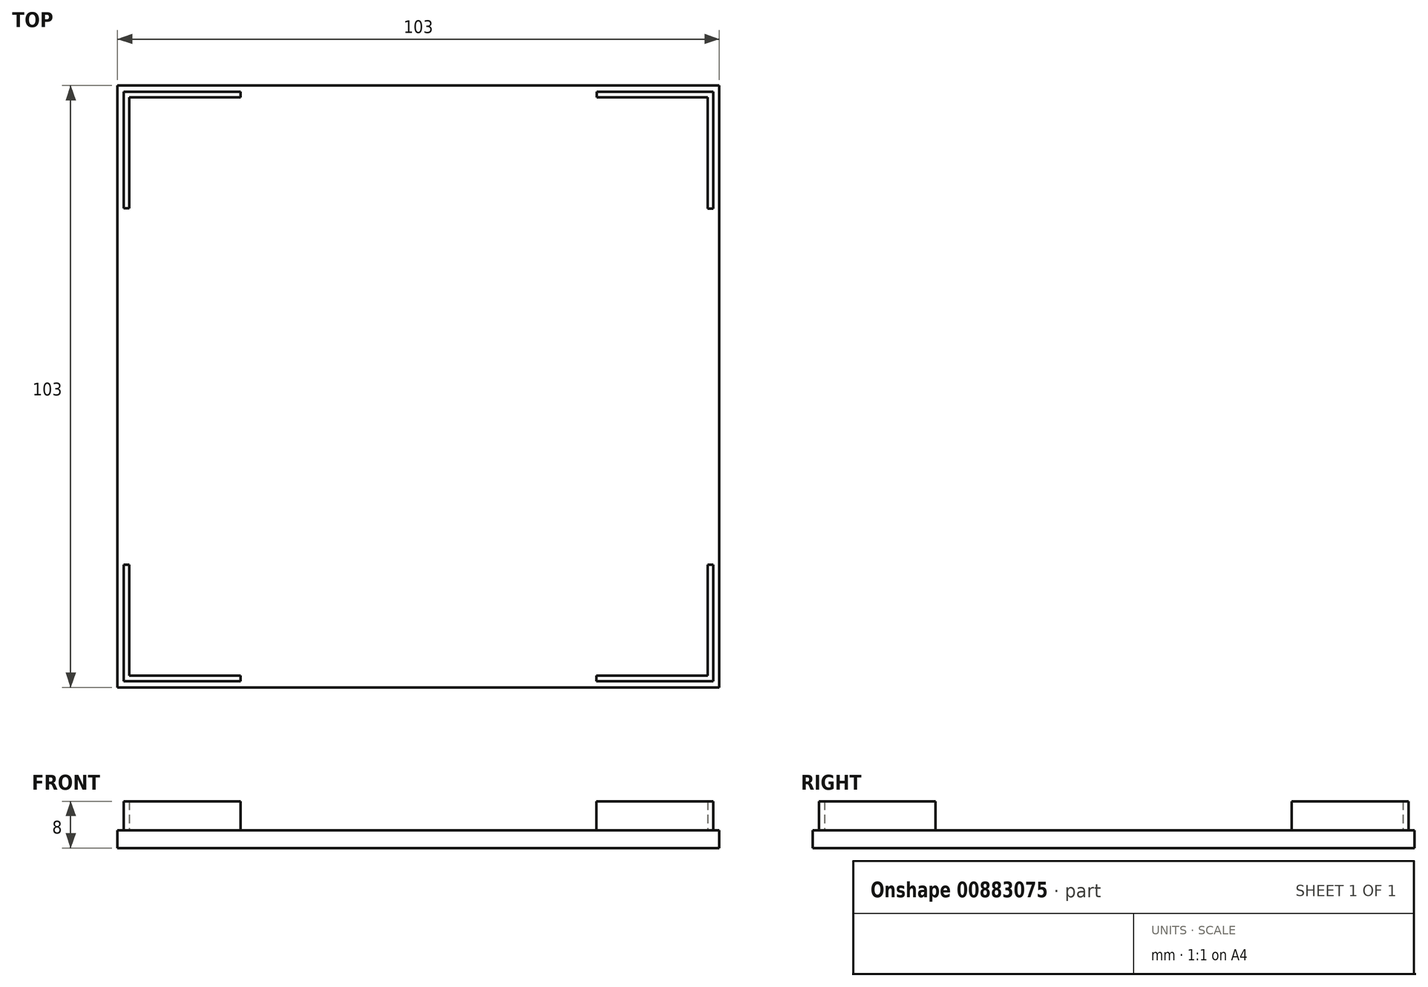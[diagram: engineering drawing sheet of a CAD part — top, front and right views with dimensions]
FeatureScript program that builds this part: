
annotation { "Feature Type Name" : "Feature", "Feature Type Description" : "" }
export const myFeature = defineFeature(function(context is Context, id is Id, definition is map)
    precondition{}
    {
        {
            var Q0;
            Q0=qCreatedBy(makeId("Top.planeOp"),FACE);
            var sketch = newSketch(context, id + "F0", { "sketchPlane" : qUnion([Q0])});
            skLineSegment(sketch, "E0.bottom", {"start": v(0, 0) * mm, "end": v(103, 0) * mm});
            skLineSegment(sketch, "E0.top", {"start": v(0, 103) * mm, "end": v(103, 103) * mm});
            skLineSegment(sketch, "E0.left", {"start": v(0, 0) * mm, "end": v(0, 103) * mm});
            skLineSegment(sketch, "E0.right", {"start": v(103, 0) * mm, "end": v(103, 103) * mm});
            skSolve(sketch);
        }
        {
            var Q0;
            Q0 = qSketchRegion(id + "F0", true);
            extrude(context, id + "F1", {"entities" : qUnion([Q0]), "depth" : 3 * mm, "offsetDistance" : 25 * mm});
        }
        {
            var Q0;
            Q0=makeQuery(id+"F1.opExtrude","CAP_FACE",FACE,{"disambiguationData":[OSD([sQuery(id+"F0.wireOp",EDGE,"E0.bottom"),sQuery(id+"F0.wireOp",EDGE,"E0.top"),sQuery(id+"F0.wireOp",EDGE,"E0.left"),sQuery(id+"F0.wireOp",EDGE,"E0.right")])],"isStart":false});
            var sketch = newSketch(context, id + "F2", { "sketchPlane" : qUnion([Q0])});
            skLineSegment(sketch, "E1.bottom", {"start": v(1.05, 2) * mm, "end": v(21.05, 2) * mm});
            skLineSegment(sketch, "E1.top", {"start": v(1.05, 1.05) * mm, "end": v(21.05, 1.05) * mm});
            skLineSegment(sketch, "E1.left", {"start": v(1.05, 2) * mm, "end": v(1.05, 1.05) * mm});
            skLineSegment(sketch, "E1.right", {"start": v(21.05, 2) * mm, "end": v(21.05, 1.05) * mm});
            skLineSegment(sketch, "E2.bottom", {"start": v(1.05, 21) * mm, "end": v(2, 21) * mm});
            skLineSegment(sketch, "E2.top", {"start": v(1.05, 2) * mm, "end": v(2, 2) * mm});
            skLineSegment(sketch, "E2.left", {"start": v(1.05, 21) * mm, "end": v(1.05, 2) * mm});
            skLineSegment(sketch, "E2.right", {"start": v(2, 21) * mm, "end": v(2, 2) * mm});
            skLineSegment(sketch, "E3.bottom", {"start": v(81.95, 2) * mm, "end": v(101.95, 2) * mm});
            skLineSegment(sketch, "E3.top", {"start": v(81.95, 1.05) * mm, "end": v(101.95, 1.05) * mm});
            skLineSegment(sketch, "E3.left", {"start": v(81.95, 2) * mm, "end": v(81.95, 1.05) * mm});
            skLineSegment(sketch, "E3.right", {"start": v(101.95, 2) * mm, "end": v(101.95, 1.05) * mm});
            skLineSegment(sketch, "E4.bottom", {"start": v(101, 21) * mm, "end": v(101.95, 21) * mm});
            skLineSegment(sketch, "E4.top", {"start": v(101, 2) * mm, "end": v(101.95, 2) * mm});
            skLineSegment(sketch, "E4.left", {"start": v(101, 21) * mm, "end": v(101, 2) * mm});
            skLineSegment(sketch, "E4.right", {"start": v(101.95, 21) * mm, "end": v(101.95, 2) * mm});
            skLineSegment(sketch, "E5.bottom", {"start": v(101.95, 101.95) * mm, "end": v(101, 101.95) * mm});
            skLineSegment(sketch, "E5.top", {"start": v(101.95, 81.95) * mm, "end": v(101, 81.95) * mm});
            skLineSegment(sketch, "E5.left", {"start": v(101.95, 101.95) * mm, "end": v(101.95, 81.95) * mm});
            skLineSegment(sketch, "E5.right", {"start": v(101, 101.95) * mm, "end": v(101, 81.95) * mm});
            skLineSegment(sketch, "E6.bottom", {"start": v(82, 101.95) * mm, "end": v(101, 101.95) * mm});
            skLineSegment(sketch, "E6.top", {"start": v(82, 101) * mm, "end": v(101, 101) * mm});
            skLineSegment(sketch, "E6.left", {"start": v(82, 101.95) * mm, "end": v(82, 101) * mm});
            skLineSegment(sketch, "E6.right", {"start": v(101, 101.95) * mm, "end": v(101, 101) * mm});
            skLineSegment(sketch, "E7.bottom", {"start": v(1.05, 101.95) * mm, "end": v(21.05, 101.95) * mm});
            skLineSegment(sketch, "E7.top", {"start": v(1.05, 101) * mm, "end": v(21.05, 101) * mm});
            skLineSegment(sketch, "E7.left", {"start": v(1.05, 101.95) * mm, "end": v(1.05, 101) * mm});
            skLineSegment(sketch, "E7.right", {"start": v(21.05, 101.95) * mm, "end": v(21.05, 101) * mm});
            skLineSegment(sketch, "E8.bottom", {"start": v(1.05, 101) * mm, "end": v(2, 101) * mm});
            skLineSegment(sketch, "E8.top", {"start": v(1.05, 82) * mm, "end": v(2, 82) * mm});
            skLineSegment(sketch, "E8.left", {"start": v(1.05, 101) * mm, "end": v(1.05, 82) * mm});
            skLineSegment(sketch, "E8.right", {"start": v(2, 101) * mm, "end": v(2, 82) * mm});
            skSolve(sketch);
        }
        {
            var Q0;
            Q0 = qSketchRegion(id + "F2", true);
            extrude(context, id + "F3", {"entities" : qUnion([Q0]), "operationType" : NewBodyOperationType.ADD, "depth" : 5 * mm, "offsetDistance" : 25 * mm});
        }
    });
